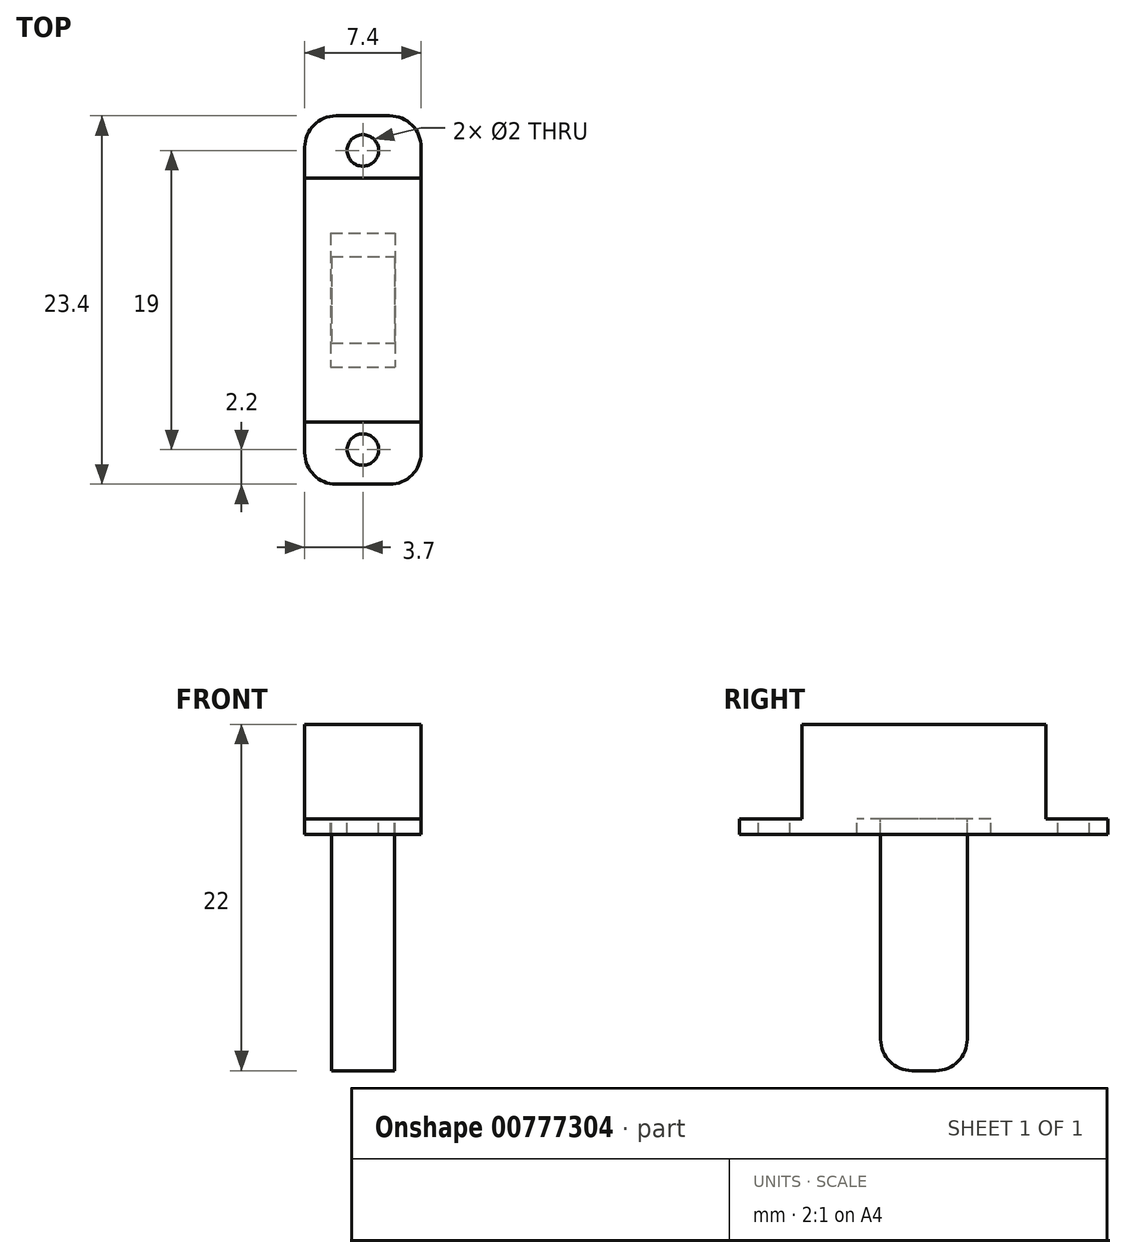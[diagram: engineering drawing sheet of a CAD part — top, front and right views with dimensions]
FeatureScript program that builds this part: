
annotation { "Feature Type Name" : "Feature", "Feature Type Description" : "" }
export const myFeature = defineFeature(function(context is Context, id is Id, definition is map)
    precondition{}
    {
        {
            var Q0;
            Q0=qCreatedBy(makeId("Top.planeOp"),FACE);
            var sketch = newSketch(context, id + "F0", { "sketchPlane" : qUnion([Q0])});
            skLineSegment(sketch, "E0.bottom", {"start": v(-3.7, 11.7) * mm, "end": v(3.7, 11.7) * mm});
            skLineSegment(sketch, "E0.top", {"start": v(-3.7, -11.7) * mm, "end": v(3.7, -11.7) * mm});
            skLineSegment(sketch, "E0.left", {"start": v(-3.7, 11.7) * mm, "end": v(-3.7, -11.7) * mm});
            skLineSegment(sketch, "E0.right", {"start": v(3.7, 11.7) * mm, "end": v(3.7, -11.7) * mm});
            skPoint(sketch, "E0.middle", {"position": v(0, 0) * mm});
            skLineSegment(sketch, "E1.bottom", {"start": v(-2, 2.75) * mm, "end": v(2, 2.75) * mm});
            skLineSegment(sketch, "E1.top", {"start": v(-2, -2.75) * mm, "end": v(2, -2.75) * mm});
            skLineSegment(sketch, "E1.left", {"start": v(-2, 2.75) * mm, "end": v(-2, -2.75) * mm});
            skLineSegment(sketch, "E1.right", {"start": v(2, 2.75) * mm, "end": v(2, -2.75) * mm});
            skLineSegment(sketch, "E2.bottom", {"start": v(-2.05, 4.25) * mm, "end": v(2.05, 4.25) * mm});
            skLineSegment(sketch, "E2.top", {"start": v(-2.05, -4.25) * mm, "end": v(2.05, -4.25) * mm});
            skLineSegment(sketch, "E2.left", {"start": v(-2.05, 4.25) * mm, "end": v(-2.05, -4.25) * mm});
            skLineSegment(sketch, "E2.right", {"start": v(2.05, 4.25) * mm, "end": v(2.05, -4.25) * mm});
            skLineSegment(sketch, "E3.bottom", {"start": v(-3.7, 7.75) * mm, "end": v(3.7, 7.75) * mm});
            skLineSegment(sketch, "E3.top", {"start": v(-3.7, -7.75) * mm, "end": v(3.7, -7.75) * mm});
            skLineSegment(sketch, "E3.left", {"start": v(-3.7, 7.75) * mm, "end": v(-3.7, -7.75) * mm});
            skLineSegment(sketch, "E3.right", {"start": v(3.7, 7.75) * mm, "end": v(3.7, -7.75) * mm});
            skCircle(sketch, "E4", {"center": v(0, 9.5) * mm, "radius": 1 * mm});
            skCircle(sketch, "E5", {"center": v(0, -9.5) * mm, "radius": 1 * mm});
            skSolve(sketch);
        }
        {
            var Q0;
            Q0=makeQuery(id+"F0.imprint","IMPRINT",FACE,{"disambiguationData":[TD([[makeQuery(id+"F0.imprint","IMPRINT",EDGE,{"derivedFrom":sQuery(id+"F0.wireOp",EDGE,"E1.bottom")}),-1.0]])]});
            extrude(context, id + "F1", {"entities" : qUnion([Q0]), "oppositeDirection" : true, "depth" : 16 * mm, "offsetDistance" : 25 * mm});
        }
        {
            var Q0;
            Q0=makeQuery(id+"F0.imprint","IMPRINT",FACE,{"disambiguationData":[TD([[makeQuery(id+"F0.imprint","IMPRINT",EDGE,{"derivedFrom":sQuery(id+"F0.wireOp",EDGE,"E2.bottom")}),1.0]])]});
            var Q1;
            {var subQ2=sQuery(id+"F0.wireOp",EDGE,"E0.top");Q1=makeQuery(id+"F0.imprint","IMPRINT",FACE,{"disambiguationData":[TD([[makeQuery(id+"F0.imprint","IMPRINT",EDGE,{"derivedFrom":subQ2}),1.0]])]});}
            var Q2;
            {var subQ2=sQuery(id+"F0.wireOp",EDGE,"E0.bottom");Q2=makeQuery(id+"F0.imprint","IMPRINT",FACE,{"disambiguationData":[TD([[makeQuery(id+"F0.imprint","IMPRINT",EDGE,{"derivedFrom":subQ2}),-1.0]])]});}
            extrude(context, id + "F2", {"entities" : qUnion([Q0, Q1, Q2]), "oppositeDirection" : true, "depth" : 1 * mm, "offsetDistance" : 25 * mm});
        }
        {
            var Q0;
            Q0=makeQuery(id+"F2.opExtrude","SWEPT_EDGE",EDGE,{"disambiguationData":[OSD([sQuery(id+"F0.wireOp",EDGE,"E0.bottom"),sQuery(id+"F0.wireOp",EDGE,"E0.right")])]});
            var Q1;
            Q1=makeQuery(id+"F2.opExtrude","SWEPT_EDGE",EDGE,{"disambiguationData":[OSD([sQuery(id+"F0.wireOp",EDGE,"E0.bottom"),sQuery(id+"F0.wireOp",EDGE,"E0.left")])]});
            var Q2;
            Q2=makeQuery(id+"F2.opExtrude","SWEPT_EDGE",EDGE,{"disambiguationData":[OSD([sQuery(id+"F0.wireOp",EDGE,"E0.top"),sQuery(id+"F0.wireOp",EDGE,"E0.right")])]});
            var Q3;
            Q3=makeQuery(id+"F2.opExtrude","SWEPT_EDGE",EDGE,{"disambiguationData":[OSD([sQuery(id+"F0.wireOp",EDGE,"E0.top"),sQuery(id+"F0.wireOp",EDGE,"E0.left")])]});
            fillet(context, id + "F3", {"entities" : qUnion([Q0, Q1, Q2, Q3]), "radius" : 2 * mm, "tangentPropagation" : true, "allowEdgeOverflow" : false});
        }
        {
            var Q0;
            Q0=makeQuery(id+"F0.imprint","IMPRINT",FACE,{"disambiguationData":[TD([[makeQuery(id+"F0.imprint","IMPRINT",EDGE,{"derivedFrom":sQuery(id+"F0.wireOp",EDGE,"E2.bottom")}),1.0]])]});
            var Q1;
            Q1=makeQuery(id+"F0.imprint","IMPRINT",FACE,{"disambiguationData":[TD([[makeQuery(id+"F0.imprint","IMPRINT",EDGE,{"derivedFrom":sQuery(id+"F0.wireOp",EDGE,"E1.bottom")}),1.0]])]});
            var Q2;
            Q2=makeQuery(id+"F0.imprint","IMPRINT",FACE,{"disambiguationData":[TD([[makeQuery(id+"F0.imprint","IMPRINT",EDGE,{"derivedFrom":sQuery(id+"F0.wireOp",EDGE,"E1.bottom")}),-1.0]])]});
            extrude(context, id + "F4", {"entities" : qUnion([Q0, Q1, Q2]), "operationType" : NewBodyOperationType.ADD, "depth" : 6 * mm, "offsetDistance" : 25 * mm});
        }
        {
            var Q0;
            Q0=makeQuery(id+"F1.opExtrude","CAP_EDGE",EDGE,{"disambiguationData":[OSD([sQuery(id+"F0.wireOp",EDGE,"E1.bottom")])],"isStart":false});
            var Q1;
            Q1=makeQuery(id+"F1.opExtrude","CAP_EDGE",EDGE,{"disambiguationData":[OSD([sQuery(id+"F0.wireOp",EDGE,"E1.top")])],"isStart":false});
            fillet(context, id + "F5", {"entities" : qUnion([Q0, Q1]), "radius" : 2 * mm, "tangentPropagation" : true, "allowEdgeOverflow" : false});
        }
    });
